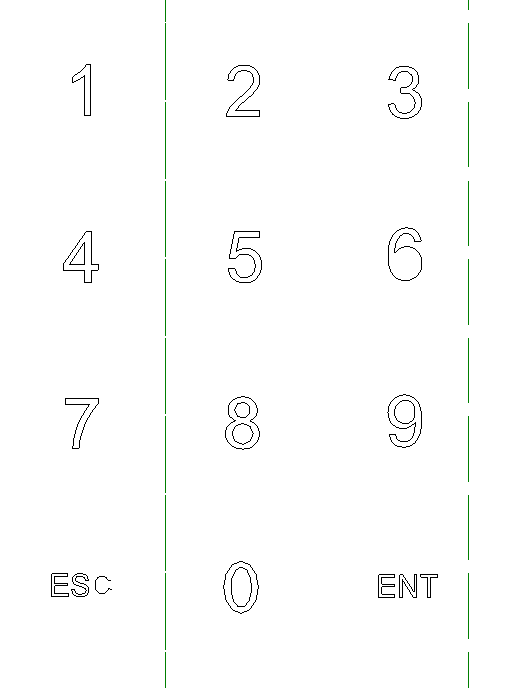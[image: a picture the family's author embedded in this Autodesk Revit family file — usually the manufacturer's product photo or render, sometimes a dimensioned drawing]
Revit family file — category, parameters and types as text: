
# Revit family: STS-708_RV17_LOD_400
name_source: partatom
category: Электрооборудование
revit_build: Autodesk Revit 2017 (Build: 20170118_1100(x64)
units: mm (PartAtom-declared; Revit-internal decimal feet)

## family parameters
Всегда вертикально = Да
Конфигурация панели = Два столбца, слева направо
На основе рабочей плоскости = Нет
Общий = Нет
При загрузке вырезать с полостями = Нет
Размер круглого соединителя = Использовать диаметр
Тип детали = Щит
Точка расчета площади = Нет

## types (1)
- STS-708
    ADSK_URL страницы изделия = https://stilsoft.ru
    ADSK_Единица измерения = шт.
    ADSK_Завод-изготовитель = ООО «Основа Безопасности»
    ADSK_Количество = 1
    ADSK_Марка = СТВФ.431295.002
    ADSK_Масса = 0.25
    ADSK_Наименование = STS-708
    ADSK_Размер_Высота = 108 мм
    ADSK_Размер_Глубина = 35 мм
    ADSK_Размер_Ширина = 87 мм
    Время считывания проксимити-карт, не более, мс = 200
    Идентификаторы = Em - Marin
    Информационные интерфейсы = Wiegand 26-42
    Кодировка = Manchester 64-bit
    Напряжение = 12
    Номинальная дальность считывания = 1-7 (зависит от
идентификатора доступа)
    Потребляемый ток, не более, А = 0.08
    Удаленность от контроллера Wiegand 42, не более, м = 100 мм
    Частота, кГц = 125
